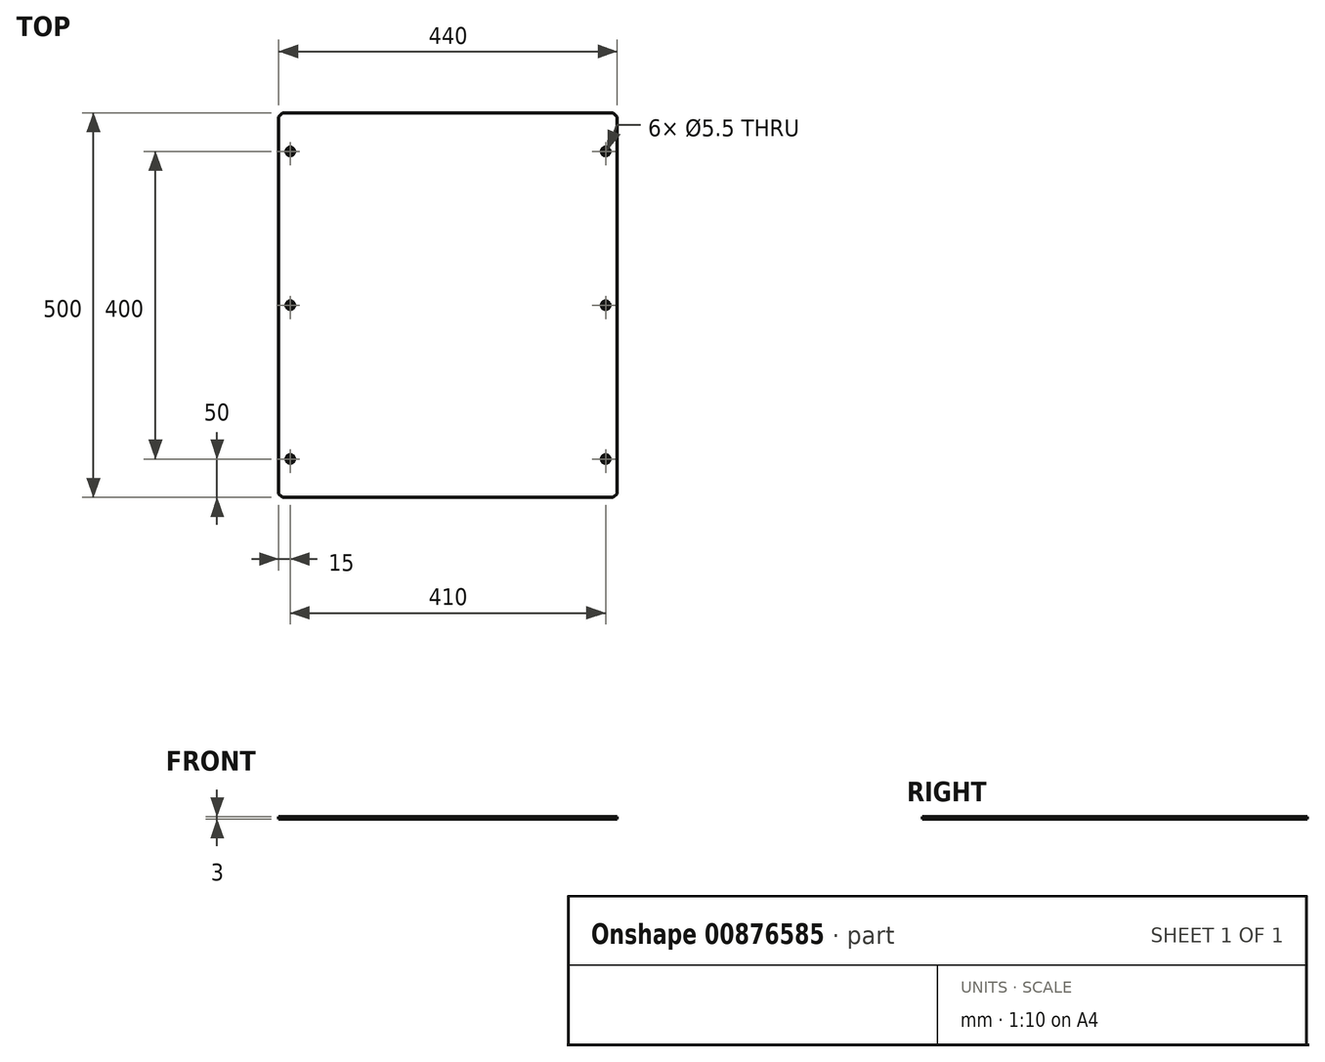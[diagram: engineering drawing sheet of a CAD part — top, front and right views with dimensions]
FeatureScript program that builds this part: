
annotation { "Feature Type Name" : "Feature", "Feature Type Description" : "" }
export const myFeature = defineFeature(function(context is Context, id is Id, definition is map)
    precondition{}
    {
        {
            var Q0;
            Q0=qCreatedBy(makeId("Top.planeOp"),FACE);
            var sketch = newSketch(context, id + "F0", { "sketchPlane" : qUnion([Q0])});
            skLineSegment(sketch, "E0.bottom", {"start": v(0, 0) * mm, "end": v(440, 0) * mm});
            skLineSegment(sketch, "E0.top", {"start": v(0, 500) * mm, "end": v(440, 500) * mm});
            skLineSegment(sketch, "E0.left", {"start": v(0, 0) * mm, "end": v(0, 500) * mm});
            skLineSegment(sketch, "E0.right", {"start": v(440, 0) * mm, "end": v(440, 500) * mm});
            skLineSegment(sketch, "E1", {"start": v(15, 500) * mm, "end": v(15, 0) * mm, "construction": true});
            skLineSegment(sketch, "E2", {"start": v(220, 500) * mm, "end": v(220, 0) * mm, "construction": true});
            skPoint(sketch, "E3", {"position": v(15, 450) * mm});
            skPoint(sketch, "E4", {"position": v(15, 250) * mm});
            skPoint(sketch, "E5", {"position": v(15, 50) * mm});
            skPoint(sketch, "E6.MirrorP", {"position": v(425, 450) * mm});
            skPoint(sketch, "E7.MirrorP", {"position": v(425, 250) * mm});
            skPoint(sketch, "E8.MirrorP", {"position": v(425, 50) * mm});
            skLineSegment(sketch, "E9.MirrorCS", {"start": v(425, 500) * mm, "end": v(425, 0) * mm, "construction": true});
            skSolve(sketch);
        }
        {
            var Q0;
            Q0=makeQuery(id+"F0.imprint","IMPRINT",FACE,{"disambiguationData":[TD([[makeQuery(id+"F0.imprint","IMPRINT",EDGE,{"derivedFrom":sQuery(id+"F0.wireOp",EDGE,"E0.bottom")}),1.0]])]});
            extrude(context, id + "F1", {"entities" : qUnion([Q0]), "oppositeDirection" : true, "depth" : 3 * mm, "offsetDistance" : 25 * mm});
        }
        {
            var Q0;
            Q0=sQuery(id+"F0.wireOp",VERTEX,"E8.MirrorP");
            var Q1;
            Q1=sQuery(id+"F0.wireOp",VERTEX,"E7.MirrorP");
            var Q2;
            Q2=sQuery(id+"F0.wireOp",VERTEX,"E6.MirrorP");
            var Q3;
            Q3=sQuery(id+"F0.wireOp",VERTEX,"E3");
            var Q4;
            Q4=sQuery(id+"F0.wireOp",VERTEX,"E4");
            var Q5;
            Q5=sQuery(id+"F0.wireOp",VERTEX,"E5");
            var Q6;
            Q6=makeQuery(id+"F1.opExtrude","SWEPT_BODY",BODY,{"disambiguationData":[OSD([sQuery(id+"F0.wireOp",EDGE,"E0.bottom"),sQuery(id+"F0.wireOp",EDGE,"E0.top"),sQuery(id+"F0.wireOp",EDGE,"E0.left"),sQuery(id+"F0.wireOp",EDGE,"E0.right")])]});
            hole(context, id + "F2", {"style" : HoleStyle.C_SINK, "endStyle" : HoleEndStyle.THROUGH, "standardTappedOrClearance" : lookupTablePath({ "fit" : "Normal", "standard" : "ISO", "size" : "M5", "type" : "Clearance" }), "standardBlindInLast" : lookupTablePath({ "fit" : "Normal", "standard" : "ISO", "size" : "M5", "type" : "Clearance" }), "holeDiameter" : 5.5 * mm, "cSinkDiameter" : 11.2 * mm, "cSinkAngle" : 90 * degree, "majorDiameter" : 5 * mm, "isTappedThrough" : true, "tappedDepth" : 12 * mm, "tapClearance" : 3, "locations" : qUnion([Q0, Q1, Q2, Q3, Q4, Q5]), "scope" : qUnion([Q6])});
        }
        {
            var Q0;
            Q0=makeQuery(id+"F1.opExtrude","SWEPT_EDGE",EDGE,{"disambiguationData":[OSD([sQuery(id+"F0.wireOp",EDGE,"E0.bottom"),sQuery(id+"F0.wireOp",EDGE,"E0.left")])]});
            var Q1;
            Q1=makeQuery(id+"F1.opExtrude","SWEPT_EDGE",EDGE,{"disambiguationData":[OSD([sQuery(id+"F0.wireOp",EDGE,"E0.bottom"),sQuery(id+"F0.wireOp",EDGE,"E0.right")])]});
            var Q2;
            Q2=makeQuery(id+"F1.opExtrude","SWEPT_EDGE",EDGE,{"disambiguationData":[OSD([sQuery(id+"F0.wireOp",EDGE,"E0.top"),sQuery(id+"F0.wireOp",EDGE,"E0.right")])]});
            var Q3;
            Q3=makeQuery(id+"F1.opExtrude","SWEPT_EDGE",EDGE,{"disambiguationData":[OSD([sQuery(id+"F0.wireOp",EDGE,"E0.top"),sQuery(id+"F0.wireOp",EDGE,"E0.left")])]});
            chamfer(context, id + "F3", {"entities" : qUnion([Q0, Q1, Q2, Q3]), "width" : 5 * mm, "tangentPropagation" : true});
        }
    });
